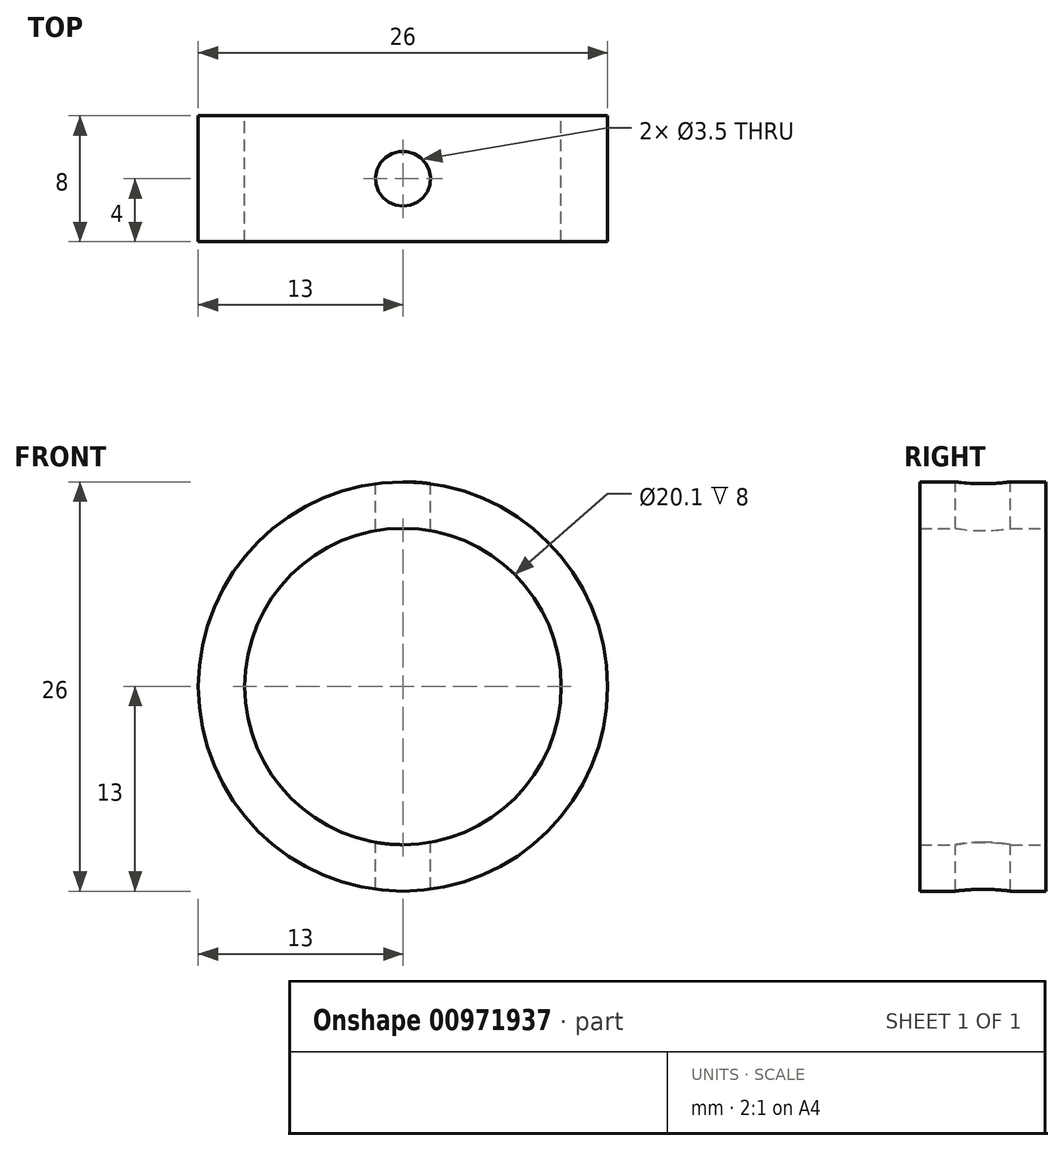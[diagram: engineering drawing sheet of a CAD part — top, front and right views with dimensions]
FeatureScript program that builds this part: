
annotation { "Feature Type Name" : "Feature", "Feature Type Description" : "" }
export const myFeature = defineFeature(function(context is Context, id is Id, definition is map)
    precondition{}
    {
        {
            var Q0;
            Q0=qCreatedBy(makeId("Front.planeOp"),FACE);
            var sketch = newSketch(context, id + "F0", { "sketchPlane" : qUnion([Q0])});
            skCircle(sketch, "E0", {"center": v(0, 0) * mm, "radius": 10.05 * mm});
            skCircle(sketch, "E1", {"center": v(0, 0) * mm, "radius": 13 * mm});
            skSolve(sketch);
        }
        {
            var Q0;
            Q0=makeQuery(id+"F0.imprint","IMPRINT",FACE,{"disambiguationData":[TD([[makeQuery(id+"F0.imprint","IMPRINT",EDGE,{"derivedFrom":sQuery(id+"F0.wireOp",EDGE,"E0")}),-1.0]])]});
            extrude(context, id + "F1", {"entities" : qUnion([Q0]), "depth" : 8 * mm, "offsetDistance" : 25 * mm});
        }
        {
            var Q0;
            Q0=qCreatedBy(makeId("Top.planeOp"),FACE);
            cPlane(context, id + "F2", {"entities" : qUnion([Q0]), "cplaneType" : CPlaneType.OFFSET, "offset" : 13 * mm, "width" : 150 * mm, "height" : 150 * mm});
        }
        {
            var Q0;
            Q0=qCreatedBy(id+"F2.planeOp",FACE);
            var sketch = newSketch(context, id + "F3", { "sketchPlane" : qUnion([Q0])});
            skPoint(sketch, "E2", {"position": v(0, -4) * mm});
            skSolve(sketch);
        }
        {
            var Q0;
            Q0=sQuery(id+"F3.wireOp",VERTEX,"E2");
            var Q1;
            Q1=makeQuery(id+"F1.opExtrude","SWEPT_BODY",BODY,{"disambiguationData":[OSD([sQuery(id+"F0.wireOp",EDGE,"E0"),sQuery(id+"F0.wireOp",EDGE,"E1")])]});
            hole(context, id + "F4", {"style" : HoleStyle.SIMPLE, "endStyle" : HoleEndStyle.THROUGH, "standardTappedOrClearance" : lookupTablePath({ "standard" : "ISO", "engagement" : "75%", "pitch" : "0.5 mm", "size" : "M4", "type" : "Tapped" }), "standardBlindInLast" : lookupTablePath({ "standard" : "ISO", "fit" : "Normal", "engagement" : "75%", "pitch" : "0.5 mm", "size" : "M4", "type" : "Clearance & tapped" }), "holeDiameter" : 3.5 * mm, "majorDiameter" : 4 * mm, "showTappedDepth" : true, "isTappedThrough" : true, "tappedDepth" : 12.6 * mm, "tapClearance" : 3, "startFromSketch" : true, "locations" : qUnion([Q0]), "scope" : qUnion([Q1])});
        }
    });
